# Revit family: Electrical-Teknion-MXPFP_Flush_Power_Module-R2023
name_source: partatom
category: Furniture
units: mm (PartAtom-declared; Revit-internal decimal feet)

## family parameters
Always vertical = Yes
Cut with Voids When Loaded = No
Enable Cutting in Views = No
OmniClass Number = 23.40.20.00
OmniClass Title = General Furniture and Specialties
Render Appearance Source = Family Geometry
Room Calculation Point = No
Shared = Yes
Work Plane-Based = No

## types (3) — shared parameters
Assembly Code = E2020200
Manufacturer = Teknion
Manufacturer Fax = 416.661.4586
Part Number = MXPFP
Product Documentation Link = http://www.teknion.com
Product Line = Electrical/Accesoriesl
Product Page URL = http://www.teknion.com
Series = Expansion Meeting
Sustainability Data = https://www.teknion.com
URL = www.teknion.com
Unit Weight URL = http://www.teknion.com
Warranty = http://www.teknion.com
zero-valued in all types: Default Elevation

## per-type parameters (varying)
| type | 2D - T | C - Circular | Description | Model | R - Rectangular | T - Rectangular With Pass Through |
| Circular Faceplate | No | Yes | Flush Power Module, Standard Plug-In, Circular Faceplate Style, Dual Electrical Cut Out | MXPFP_CAH__ | No | No |
| Rectangular With Pass Through Faceplate | Yes | No | Flush Power Module, Standard Plug-In, Rectangular With Pass Through Faceplate Style, Triple Electrical Cut Out | MXPFP_TAJ__ | No | Yes |
| Rectangular Faceplate | No | No | Flush Power Module, Standard Plug-In, Rectangular Faceplate Style | MXPFP_R___ | Yes | No |

## geometry (parser evidence)
native form markers: Sweep x14
no freeform markers — native parametric forms only
